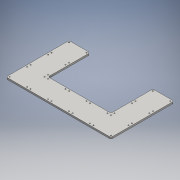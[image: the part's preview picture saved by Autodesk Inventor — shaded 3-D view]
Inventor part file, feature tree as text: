
AUTODESK INVENTOR PART (.ipt)
format: ipt  version: 2016 (Build 200138000, 138)  size: 224,768 bytes
history: native  units: mm
features: extrude x1, fillet x1, sketch x1
ambient origin geometry x8: Origin, YZ Plane, XZ Plane, XY Plane, X Axis, Y Axis, Z Axis, Center Point
bodies: Solid1 (feature_tree)
feature tree (3):
  extrude  "Extrusion1"  Depth=60.0mm
  fillet  "Fillet1"  Radius=120.0mm
  sketch  "Sketch1"  dims[d0=180.0mm d1=60.0mm d2=120.0mm d3=180.0mm d4=60.0mm d5=60.0mm d6=60.0mm d7=60.0mm d8=60.0mm d9=50.0mm d10=50.0mm d11=50.0mm d12=50.0mm d13=50.0mm d14=50.0mm d15=50.0mm d16=50.0mm d17=50.0mm d18=50.0mm d19=50.0mm d20=50.0mm d21=50.0mm d22=50.0mm d23=50.0mm d24=50.0mm d25=50.0mm d26=50.0mm d27=3.0mm d28=3.0mm d29=3.0mm d30=3.0mm d31=3.0mm d32=3.0mm d33=3.0mm d34=3.0mm d35=3.0mm d36=3.0mm d37=3.0mm d38=3.0mm d39=3.0mm d40=3.0mm d41=3.0mm d42=3.0mm d43=3.0mm d44=3.0mm d45=3.0mm d46=3.0mm d47=3.0mm d48=3.0mm d49=3.0mm d50=3.0mm d51=3.0mm d52=3.0mm d53=3.0mm d54=3.0mm d55=3.0mm d56=3.0mm d57=3.0mm d58=3.0mm d59=3.0mm d60=3.0mm d61=3.0mm d62=3.0mm d63=5.0mm d64=0.0mm d65=5.0mm]
